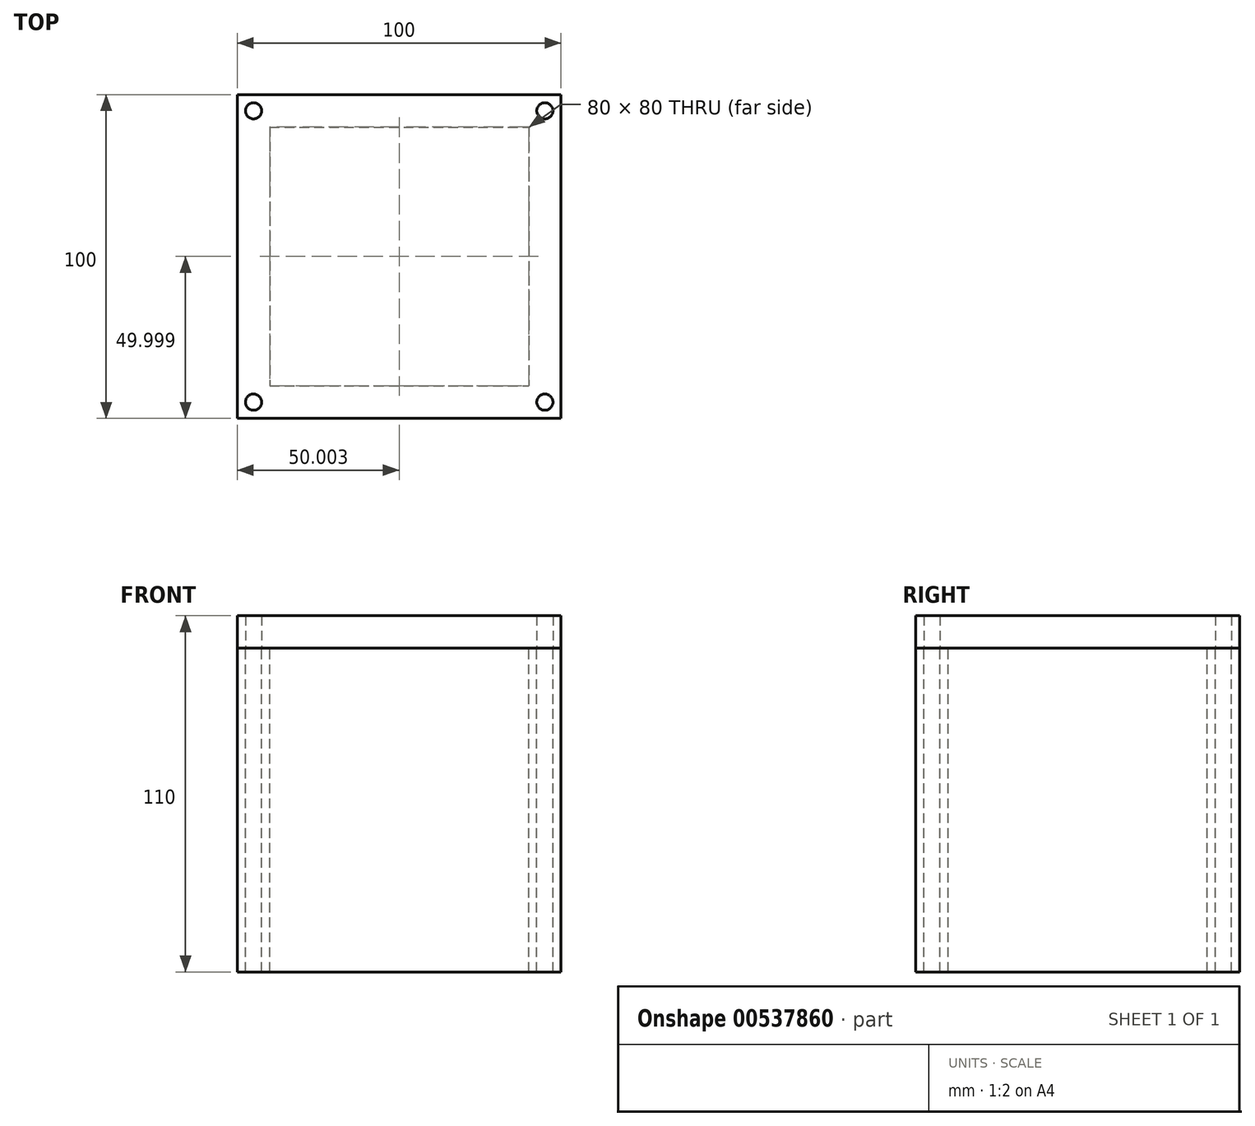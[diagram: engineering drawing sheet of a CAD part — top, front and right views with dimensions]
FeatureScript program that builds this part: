
annotation { "Feature Type Name" : "Feature", "Feature Type Description" : "" }
export const myFeature = defineFeature(function(context is Context, id is Id, definition is map)
    precondition{}
    {
        {
            var Q0;
            Q0=qCreatedBy(makeId("Top.planeOp"),FACE);
            var sketch = newSketch(context, id + "F0", { "sketchPlane" : qUnion([Q0])});
            skLineSegment(sketch, "E0.bottom", {"start": v(-45, 59.53) * mm, "end": v(55, 59.53) * mm});
            skLineSegment(sketch, "E0.top", {"start": v(-45, -40.47) * mm, "end": v(55, -40.47) * mm});
            skLineSegment(sketch, "E0.left", {"start": v(-45, 59.53) * mm, "end": v(-45, -40.47) * mm});
            skLineSegment(sketch, "E0.right", {"start": v(55, 59.53) * mm, "end": v(55, -40.47) * mm});
            skSolve(sketch);
        }
        {
            var Q0;
            Q0 = qSketchRegion(id + "F0", true);
            extrude(context, id + "F1", {"entities" : qUnion([Q0]), "depth" : 100 * mm, "offsetDistance" : 25 * mm});
        }
        {
            var Q0;
            Q0=makeQuery(id+"F1.opExtrude","CAP_FACE",FACE,{"disambiguationData":[OSD([sQuery(id+"F0.wireOp",EDGE,"E0.bottom"),sQuery(id+"F0.wireOp",EDGE,"E0.top"),sQuery(id+"F0.wireOp",EDGE,"E0.left"),sQuery(id+"F0.wireOp",EDGE,"E0.right")])],"isStart":false});
            var sketch = newSketch(context, id + "F2", { "sketchPlane" : qUnion([Q0])});
            skLineSegment(sketch, "E1.bottom", {"start": v(-35, 49.53) * mm, "end": v(45, 49.53) * mm});
            skLineSegment(sketch, "E1.top", {"start": v(-35, -30.47) * mm, "end": v(45, -30.47) * mm});
            skLineSegment(sketch, "E1.left", {"start": v(-35, 49.53) * mm, "end": v(-35, -30.47) * mm});
            skLineSegment(sketch, "E1.right", {"start": v(45, 49.53) * mm, "end": v(45, -30.47) * mm});
            skSolve(sketch);
        }
        {
            var Q0;
            Q0 = qSketchRegion(id + "F2", true);
            extrude(context, id + "F3", {"entities" : qUnion([Q0]), "operationType" : NewBodyOperationType.REMOVE, "endBound" : BoundingType.THROUGH_ALL, "oppositeDirection" : true, "depth" : 100 * mm, "offsetDistance" : 25 * mm});
        }
        {
            var Q0;
            Q0=makeQuery(id+"F1.opExtrude","CAP_FACE",FACE,{"disambiguationData":[OSD([sQuery(id+"F0.wireOp",EDGE,"E0.bottom"),sQuery(id+"F0.wireOp",EDGE,"E0.top"),sQuery(id+"F0.wireOp",EDGE,"E0.left"),sQuery(id+"F0.wireOp",EDGE,"E0.right")])],"isStart":false});
            var sketch = newSketch(context, id + "F4", { "sketchPlane" : qUnion([Q0])});
            skCircle(sketch, "E2", {"center": v(-40, 54.53) * mm, "radius": 2.5 * mm});
            skCircle(sketch, "E3", {"center": v(50, 54.53) * mm, "radius": 2.5 * mm});
            skCircle(sketch, "E4", {"center": v(-40, -35.47) * mm, "radius": 2.5 * mm});
            skCircle(sketch, "E5", {"center": v(50, -35.47) * mm, "radius": 2.5 * mm});
            skSolve(sketch);
        }
        {
            var Q0;
            Q0 = qSketchRegion(id + "F4", true);
            extrude(context, id + "F5", {"entities" : qUnion([Q0]), "operationType" : NewBodyOperationType.REMOVE, "endBound" : BoundingType.THROUGH_ALL, "oppositeDirection" : true, "depth" : 25 * mm, "offsetDistance" : 25 * mm});
        }
        {
            var Q0;
            Q0=makeQuery(id+"F1.opExtrude","CAP_FACE",FACE,{"disambiguationData":[OSD([sQuery(id+"F0.wireOp",EDGE,"E0.bottom"),sQuery(id+"F0.wireOp",EDGE,"E0.top"),sQuery(id+"F0.wireOp",EDGE,"E0.left"),sQuery(id+"F0.wireOp",EDGE,"E0.right")])],"isStart":false});
            var sketch = newSketch(context, id + "F6", { "sketchPlane" : qUnion([Q0])});
            skLineSegment(sketch, "E6.0", {"start": v(-45, 59.53) * mm, "end": v(55, 59.53) * mm});
            skLineSegment(sketch, "E7.0", {"start": v(-45, -40.47) * mm, "end": v(55, -40.47) * mm});
            skLineSegment(sketch, "E8.0", {"start": v(-45, 59.53) * mm, "end": v(-45, -40.47) * mm});
            skLineSegment(sketch, "E9.0", {"start": v(55, 59.53) * mm, "end": v(55, -40.47) * mm});
            skCircle(sketch, "E10.0", {"center": v(-40, 54.53) * mm, "radius": 2.5 * mm});
            skCircle(sketch, "E11.0", {"center": v(-40, -35.47) * mm, "radius": 2.5 * mm});
            skCircle(sketch, "E11.1", {"center": v(50, -35.47) * mm, "radius": 2.5 * mm});
            skCircle(sketch, "E11.2", {"center": v(50, 54.53) * mm, "radius": 2.5 * mm});
            skSolve(sketch);
        }
        {
            var Q0;
            Q0 = qSketchRegion(id + "F6", true);
            extrude(context, id + "F7", {"entities" : qUnion([Q0]), "depth" : 10 * mm, "offsetDistance" : 25 * mm});
        }
    });
